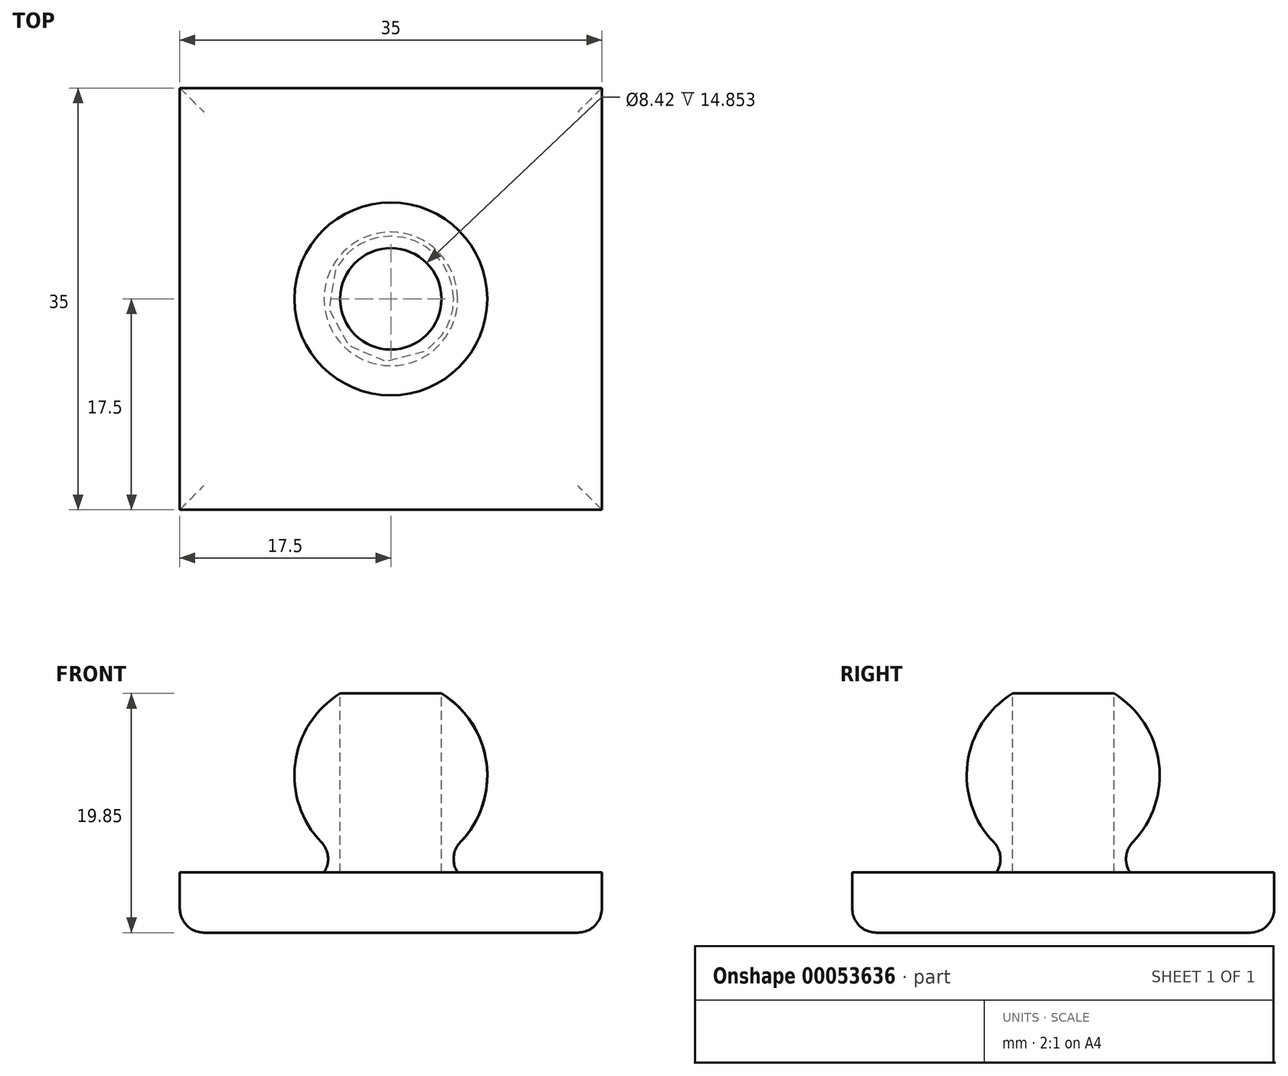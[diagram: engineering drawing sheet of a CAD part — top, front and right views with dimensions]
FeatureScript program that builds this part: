
annotation { "Feature Type Name" : "Feature", "Feature Type Description" : "" }
export const myFeature = defineFeature(function(context is Context, id is Id, definition is map)
    precondition{}
    {
        {
            var Q0;
            Q0=qCreatedBy(makeId("Front.planeOp"),FACE);
            var sketch = newSketch(context, id + "F0", { "sketchPlane" : qUnion([Q0])});
            skArc(sketch, "E0", {"start": v(0, 4.09) * mm, "mid": v(0.5, 4.1) * mm, "end": v(1, 4.15) * mm});
            skLineSegment(sketch, "E1", {"start": v(5.54, 4.04) * mm, "end": v(10.12, -2.8) * mm});
            skLineSegment(sketch, "E2", {"start": v(10.12, -2.8) * mm, "end": v(10.12, -5.91) * mm});
            skLineSegment(sketch, "E3", {"start": v(10.12, -5.91) * mm, "end": v(7.88, -5.91) * mm});
            skArc(sketch, "E4", {"start": v(7.88, -5.91) * mm, "mid": v(6.7, 0.67) * mm, "end": v(1, 4.15) * mm});
            skLineSegment(sketch, "E5", {"start": v(0, 10.09) * mm, "end": v(7.75, 10.09) * mm, "construction": true});
            skPoint(sketch, "E6", {"position": v(0, 20.09) * mm});
            skPoint(sketch, "E7", {"position": v(0, 10.09) * mm});
            skPoint(sketch, "E8.orphan", {"position": v(-7.75, 10.09) * mm});
            skPoint(sketch, "E9.orphan", {"position": v(0, -5.91) * mm});
            skLineSegment(sketch, "E10", {"start": v(0, 20.09) * mm, "end": v(0, 4.09) * mm});
            skArc(sketch, "E11.trimOffspring", {"start": v(5.76, 6.54) * mm, "mid": v(7.36, 15.22) * mm, "end": v(0, 20.09) * mm});
            skLineSegment(sketch, "E12", {"start": v(0, 4.09) * mm, "end": v(0, -5.91) * mm, "construction": true});
            skPoint(sketch, "E13.visualSharp", {"position": v(4.56, 5.5) * mm});
            skArc(sketch, "E13.filletArc", {"start": v(5.76, 6.54) * mm, "mid": v(5.21, 5.33) * mm, "end": v(5.54, 4.04) * mm});
            skSolve(sketch);
        }
        {
            var Q0;
            Q0=qSketchRegion(id+"F0",true);
            var Q1;
            Q1=sQuery(id+"F0.wireOp",EDGE,"E12");
            revolve(context, id + "F1", {"entities" : qUnion([Q0]), "axis" : qUnion([Q1]), "revolveType" : RevolveType.FULL});
        }
        {
            var Q0;
            Q0=qCreatedBy(makeId("Top.planeOp"),FACE);
            var sketch = newSketch(context, id + "F2", { "sketchPlane" : qUnion([Q0])});
            skCircle(sketch, "E14", {"center": v(0, 0) * mm, "radius": 4.2 * mm});
            skSolve(sketch);
        }
        {
            var Q0;
            Q0=qSketchRegion(id+"F2",true);
            extrude(context, id + "F3", {"entities" : qUnion([Q0]), "operationType" : NewBodyOperationType.REMOVE, "endBound" : BoundingType.SYMMETRIC, "oppositeDirection" : true, "depth" : 50 * mm});
        }
        {
            var Q0;
            Q0=qCreatedBy(makeId("Right.planeOp"),FACE);
            var sketch = newSketch(context, id + "F4", { "sketchPlane" : qUnion([Q0])});
            skLineSegment(sketch, "E15.bottom", {"start": v(1, -5.91) * mm, "end": v(-1, -5.91) * mm});
            skLineSegment(sketch, "E15.left", {"start": v(1, -5.91) * mm, "end": v(1, -0.91) * mm});
            skLineSegment(sketch, "E15.right", {"start": v(-1, -5.91) * mm, "end": v(-1, -0.91) * mm});
            skArc(sketch, "E16", {"start": v(1, -0.91) * mm, "mid": v(0, 0.09) * mm, "end": v(-1, -0.91) * mm});
            skSolve(sketch);
        }
        {
            var Q0;
            Q0=qSketchRegion(id+"F4",true);
            extrude(context, id + "F5", {"entities" : qUnion([Q0]), "operationType" : NewBodyOperationType.REMOVE, "endBound" : BoundingType.SYMMETRIC, "oppositeDirection" : true, "depth" : 25 * mm});
        }
        {
            var Q0;
            Q0=qCreatedBy(makeId("Front.planeOp"),FACE);
            var sketch = newSketch(context, id + "F6", { "sketchPlane" : qUnion([Q0])});
            skLineSegment(sketch, "E17.bottom", {"start": v(-34.6, 4.04) * mm, "end": v(25.65, 4.04) * mm});
            skLineSegment(sketch, "E17.top", {"start": v(-34.6, -16.9) * mm, "end": v(25.65, -16.9) * mm});
            skLineSegment(sketch, "E17.left", {"start": v(-34.6, 4.04) * mm, "end": v(-34.6, -16.9) * mm});
            skLineSegment(sketch, "E17.right", {"start": v(25.65, 4.04) * mm, "end": v(25.65, -16.9) * mm});
            skSolve(sketch);
        }
        {
            var Q0;
            Q0=qSketchRegion(id+"F6",true);
            extrude(context, id + "F7", {"entities" : qUnion([Q0]), "operationType" : NewBodyOperationType.REMOVE, "endBound" : BoundingType.SYMMETRIC, "oppositeDirection" : true, "depth" : 25 * mm});
        }
        {
            var Q0;
            Q0=makeQuery(id+"F7.boolean.opBoolean","COPY",FACE,{"derivedFrom":makeQuery(id+"F7.opExtrude","SWEPT_FACE",FACE,{"disambiguationData":[OSD([sQuery(id+"F6.wireOp",EDGE,"E17.bottom")])]})});
            var sketch = newSketch(context, id + "F8", { "sketchPlane" : qUnion([Q0])});
            skLineSegment(sketch, "E18.rect.bottom", {"start": v(17.5, -17.5) * mm, "end": v(-17.5, -17.5) * mm});
            skLineSegment(sketch, "E18.rect.top", {"start": v(17.5, 17.5) * mm, "end": v(-17.5, 17.5) * mm});
            skLineSegment(sketch, "E18.rect.left", {"start": v(17.5, -17.5) * mm, "end": v(17.5, 17.5) * mm});
            skLineSegment(sketch, "E18.rect.right", {"start": v(-17.5, -17.5) * mm, "end": v(-17.5, 17.5) * mm});
            skPoint(sketch, "E18.rect.middle", {"position": v(0, 0) * mm});
            skSolve(sketch);
        }
        {
            var Q0;
            Q0=qSketchRegion(id+"F8",true);
            extrude(context, id + "F9", {"entities" : qUnion([Q0]), "operationType" : NewBodyOperationType.ADD, "depth" : 5 * mm});
        }
        {
            var Q0;
            Q0=makeQuery(id+"F9.opExtrude","CAP_EDGE",EDGE,{"disambiguationData":[OSD([sQuery(id+"F8.wireOp",EDGE,"E18.rect.top")])],"isStart":false});
            var Q1;
            Q1=makeQuery(id+"F9.opExtrude","CAP_EDGE",EDGE,{"disambiguationData":[OSD([sQuery(id+"F8.wireOp",EDGE,"E18.rect.right")])],"isStart":false});
            var Q2;
            Q2=makeQuery(id+"F9.opExtrude","CAP_EDGE",EDGE,{"disambiguationData":[OSD([sQuery(id+"F8.wireOp",EDGE,"E18.rect.bottom")])],"isStart":false});
            var Q3;
            Q3=makeQuery(id+"F9.opExtrude","CAP_EDGE",EDGE,{"disambiguationData":[OSD([sQuery(id+"F8.wireOp",EDGE,"E18.rect.left")])],"isStart":false});
            fillet(context, id + "F10", {"entities" : qUnion([Q0, Q1, Q2, Q3]), "radius" : 2 * mm, "tangentPropagation" : true, "allowEdgeOverflow" : false});
        }
    });
